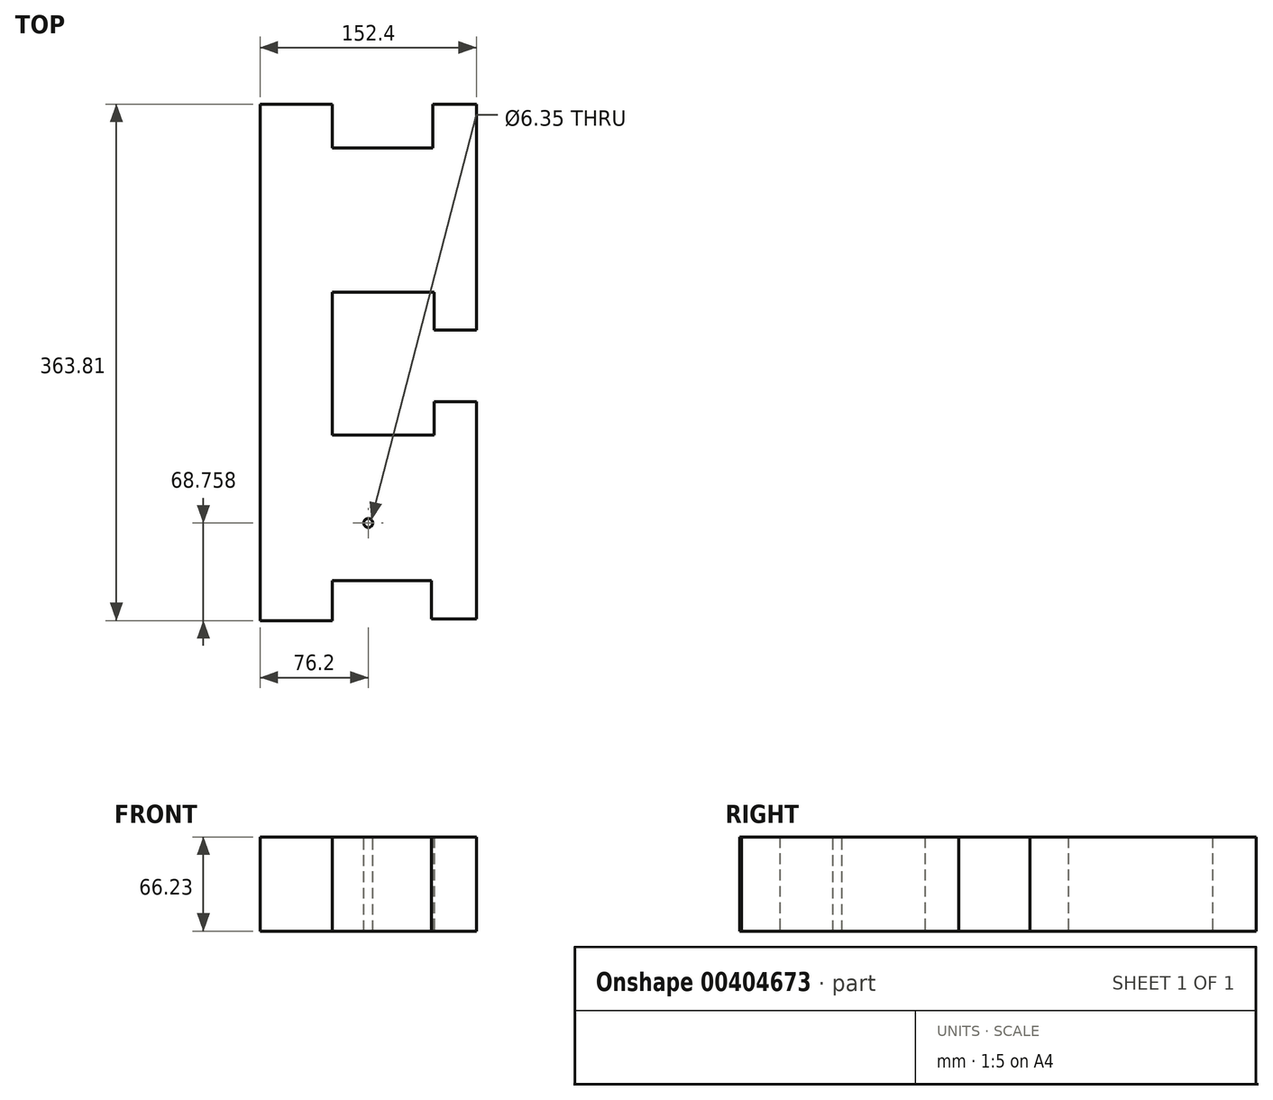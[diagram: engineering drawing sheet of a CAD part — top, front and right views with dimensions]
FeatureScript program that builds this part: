
annotation { "Feature Type Name" : "Feature", "Feature Type Description" : "" }
export const myFeature = defineFeature(function(context is Context, id is Id, definition is map)
    precondition{}
    {
        {
            var Q0;
            Q0=qCreatedBy(makeId("Top.planeOp"),FACE);
            var sketch = newSketch(context, id + "F0", { "sketchPlane" : qUnion([Q0])});
            skLineSegment(sketch, "E0.bottom", {"start": v(-25.4, -152.4) * mm, "end": v(44.45, -152.4) * mm});
            skLineSegment(sketch, "E0.top", {"start": v(-25.4, 152.4) * mm, "end": v(45.36, 152.4) * mm});
            skLineSegment(sketch, "E0.left", {"start": v(-76.2, -152.4) * mm, "end": v(-76.2, 152.4) * mm});
            skLineSegment(sketch, "E0.right", {"start": v(76.2, -152.4) * mm, "end": v(76.2, -26.4) * mm});
            skPoint(sketch, "E0.middle", {"position": v(0, 0) * mm});
            skLineSegment(sketch, "E1.left", {"start": v(-76.2, 152.4) * mm, "end": v(-76.2, -152.4) * mm});
            skLineSegment(sketch, "E1.right", {"start": v(-25.4, 50.8) * mm, "end": v(-25.4, -50.05) * mm});
            skLineSegment(sketch, "E2.top", {"start": v(-25.4, 50.8) * mm, "end": v(46.33, 50.8) * mm});
            skLineSegment(sketch, "E3.top", {"start": v(-25.4, -50.05) * mm, "end": v(46.33, -50.05) * mm});
            skLineSegment(sketch, "E3.right", {"start": v(76.2, -152.4) * mm, "end": v(76.2, -50.05) * mm});
            skLineSegment(sketch, "E4", {"start": v(76.2, 50.8) * mm, "end": v(76.2, 23.9) * mm});
            skLineSegment(sketch, "E5.right", {"start": v(46.33, 50.8) * mm, "end": v(46.33, 23.9) * mm});
            skLineSegment(sketch, "E6.top", {"start": v(46.33, 23.9) * mm, "end": v(76.2, 23.9) * mm});
            skLineSegment(sketch, "E7.top", {"start": v(46.33, -26.4) * mm, "end": v(76.2, -26.4) * mm});
            skLineSegment(sketch, "E7.left", {"start": v(46.33, -50.05) * mm, "end": v(46.33, -26.4) * mm});
            skLineSegment(sketch, "E7.right", {"start": v(76.2, -50.05) * mm, "end": v(76.2, -26.4) * mm});
            skLineSegment(sketch, "E8.trimOffspring", {"start": v(46.33, -26.4) * mm, "end": v(46.33, -50.05) * mm});
            skLineSegment(sketch, "E9.top", {"start": v(76.2, 183.14) * mm, "end": v(45.36, 183.14) * mm});
            skLineSegment(sketch, "E9.left", {"start": v(76.2, 152.4) * mm, "end": v(76.2, 183.14) * mm});
            skLineSegment(sketch, "E9.right", {"start": v(45.36, 152.4) * mm, "end": v(45.36, 183.14) * mm});
            skLineSegment(sketch, "E10.top", {"start": v(-76.2, 183.14) * mm, "end": v(-25.4, 183.14) * mm});
            skLineSegment(sketch, "E10.left", {"start": v(-76.2, 152.4) * mm, "end": v(-76.2, 183.14) * mm});
            skLineSegment(sketch, "E10.right", {"start": v(-25.4, 152.4) * mm, "end": v(-25.4, 183.14) * mm});
            skLineSegment(sketch, "E11.top", {"start": v(76.2, -179.55) * mm, "end": v(44.45, -179.55) * mm});
            skLineSegment(sketch, "E11.left", {"start": v(76.2, -152.4) * mm, "end": v(76.2, -179.55) * mm});
            skLineSegment(sketch, "E11.right", {"start": v(44.45, -152.4) * mm, "end": v(44.45, -179.55) * mm});
            skLineSegment(sketch, "E12.top", {"start": v(-76.2, -180.67) * mm, "end": v(-25.4, -180.67) * mm});
            skLineSegment(sketch, "E12.left", {"start": v(-76.2, -152.4) * mm, "end": v(-76.2, -180.67) * mm});
            skLineSegment(sketch, "E12.right", {"start": v(-25.4, -152.4) * mm, "end": v(-25.4, -180.67) * mm});
            skLineSegment(sketch, "E13.trimOffspring", {"start": v(76.2, 23.9) * mm, "end": v(76.2, 50.8) * mm});
            skLineSegment(sketch, "E14.trimOffspring", {"start": v(76.2, -26.4) * mm, "end": v(76.2, -50.05) * mm});
            skLineSegment(sketch, "E15", {"start": v(76.2, 152.4) * mm, "end": v(76.2, 50.8) * mm});
            skSolve(sketch);
        }
        {
            var Q0;
            Q0 = qSketchRegion(id + "F0", true);
            extrude(context, id + "F1", {"entities" : qUnion([Q0]), "depth" : 66.23 * mm});
        }
        {
            var Q0;
            Q0=makeQuery(id+"F1.opExtrude","CAP_FACE",FACE,{"disambiguationData":[OSD([sQuery(id+"F0.wireOp",EDGE,"E1.left"),sQuery(id+"F0.wireOp",EDGE,"E0.top"),sQuery(id+"F0.wireOp",EDGE,"E0.bottom"),sQuery(id+"F0.wireOp",EDGE,"E3.right"),sQuery(id+"F0.wireOp",EDGE,"E2.top"),sQuery(id+"F0.wireOp",EDGE,"E3.top"),sQuery(id+"F0.wireOp",EDGE,"E1.right"),sQuery(id+"F0.wireOp",EDGE,"E6.top"),sQuery(id+"F0.wireOp",EDGE,"E5.right"),sQuery(id+"F0.wireOp",EDGE,"E7.top"),sQuery(id+"F0.wireOp",EDGE,"E8.trimOffspring"),sQuery(id+"F0.wireOp",EDGE,"E9.top"),sQuery(id+"F0.wireOp",EDGE,"E9.left"),sQuery(id+"F0.wireOp",EDGE,"E9.right"),sQuery(id+"F0.wireOp",EDGE,"E10.top"),sQuery(id+"F0.wireOp",EDGE,"E10.left"),sQuery(id+"F0.wireOp",EDGE,"E10.right"),sQuery(id+"F0.wireOp",EDGE,"E11.top"),sQuery(id+"F0.wireOp",EDGE,"E11.left"),sQuery(id+"F0.wireOp",EDGE,"E11.right"),sQuery(id+"F0.wireOp",EDGE,"E12.top"),sQuery(id+"F0.wireOp",EDGE,"E12.left"),sQuery(id+"F0.wireOp",EDGE,"E12.right"),sQuery(id+"F0.wireOp",EDGE,"E13.trimOffspring"),sQuery(id+"F0.wireOp",EDGE,"E14.trimOffspring"),sQuery(id+"F0.wireOp",EDGE,"E15")])],"isStart":false});
            var sketch = newSketch(context, id + "F2", { "sketchPlane" : qUnion([Q0])});
            skCircle(sketch, "E16", {"center": v(0, 103.06) * mm, "radius": 18.58 * mm});
            skCircle(sketch, "E17", {"center": v(0, -111.91) * mm, "radius": 19.43 * mm});
            skSolve(sketch);
        }
        {
            var Q0;
            Q0=sQuery(id+"F2.wireOp",VERTEX,"E17.center");
            var Q1;
            Q1=makeQuery(id+"F1.opExtrude","SWEPT_BODY",BODY,{"disambiguationData":[OSD([sQuery(id+"F0.wireOp",EDGE,"E1.left"),sQuery(id+"F0.wireOp",EDGE,"E0.top"),sQuery(id+"F0.wireOp",EDGE,"E0.bottom"),sQuery(id+"F0.wireOp",EDGE,"E3.right"),sQuery(id+"F0.wireOp",EDGE,"E2.top"),sQuery(id+"F0.wireOp",EDGE,"E3.top"),sQuery(id+"F0.wireOp",EDGE,"E1.right"),sQuery(id+"F0.wireOp",EDGE,"E6.top"),sQuery(id+"F0.wireOp",EDGE,"E5.right"),sQuery(id+"F0.wireOp",EDGE,"E7.top"),sQuery(id+"F0.wireOp",EDGE,"E8.trimOffspring"),sQuery(id+"F0.wireOp",EDGE,"E9.top"),sQuery(id+"F0.wireOp",EDGE,"E9.left"),sQuery(id+"F0.wireOp",EDGE,"E9.right"),sQuery(id+"F0.wireOp",EDGE,"E10.top"),sQuery(id+"F0.wireOp",EDGE,"E10.left"),sQuery(id+"F0.wireOp",EDGE,"E10.right"),sQuery(id+"F0.wireOp",EDGE,"E11.top"),sQuery(id+"F0.wireOp",EDGE,"E11.left"),sQuery(id+"F0.wireOp",EDGE,"E11.right"),sQuery(id+"F0.wireOp",EDGE,"E12.top"),sQuery(id+"F0.wireOp",EDGE,"E12.left"),sQuery(id+"F0.wireOp",EDGE,"E12.right"),sQuery(id+"F0.wireOp",EDGE,"E13.trimOffspring"),sQuery(id+"F0.wireOp",EDGE,"E14.trimOffspring"),sQuery(id+"F0.wireOp",EDGE,"E15")])]});
            hole(context, id + "F3", {"style" : HoleStyle.SIMPLE, "endStyle" : HoleEndStyle.THROUGH, "holeDiameter" : 6.35 * mm, "isTappedThrough" : true, "tappedDepth" : 12.7 * mm, "tapClearance" : 3, "locations" : qUnion([Q0]), "scope" : qUnion([Q1])});
        }
    });
